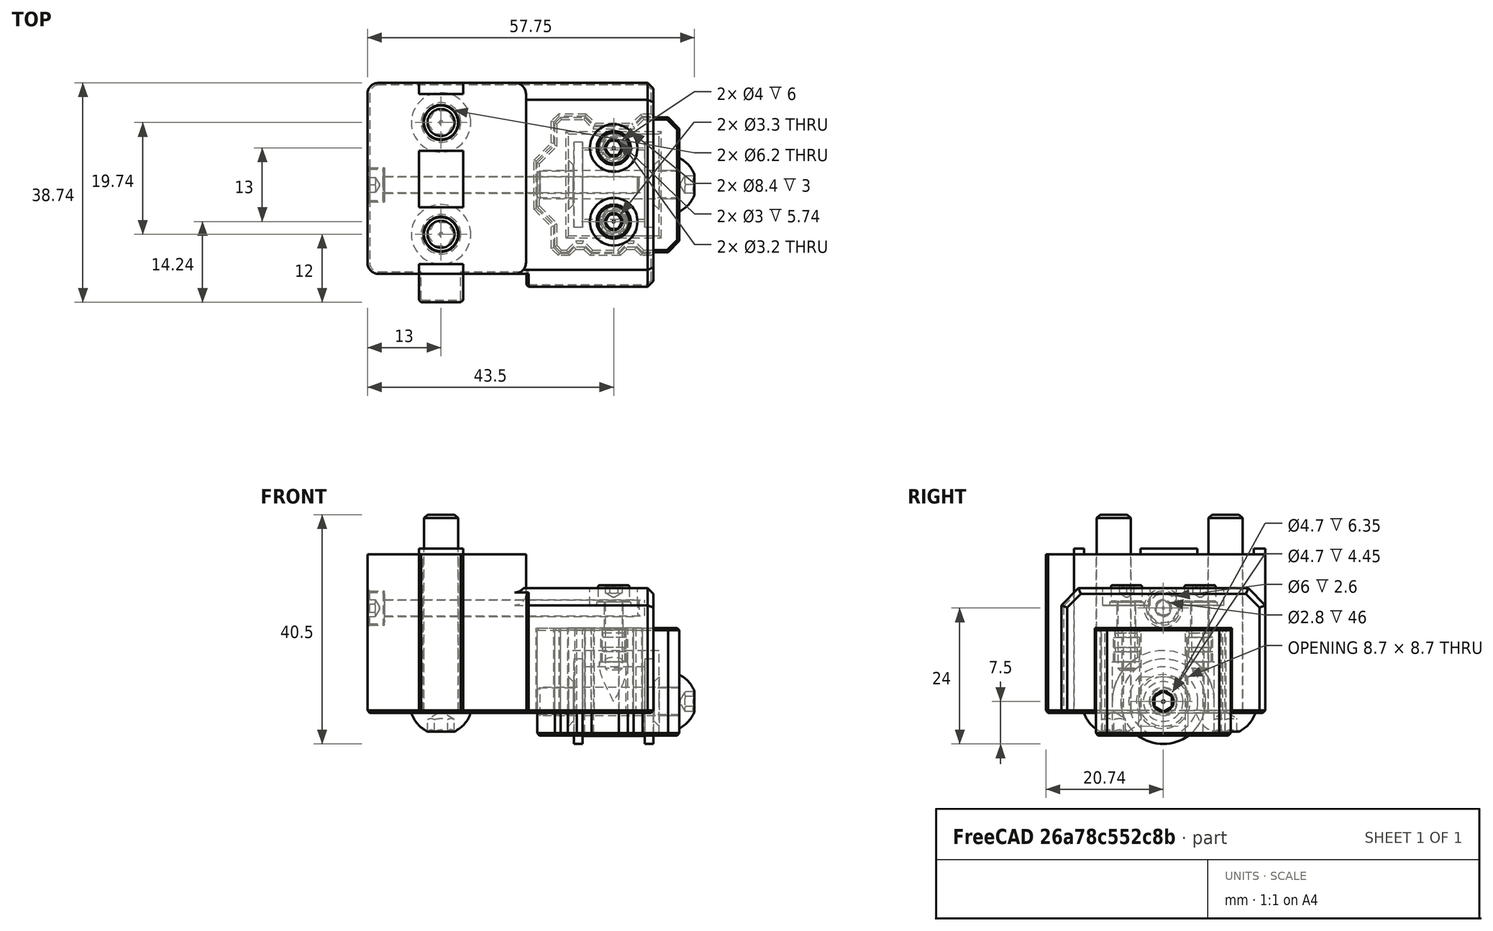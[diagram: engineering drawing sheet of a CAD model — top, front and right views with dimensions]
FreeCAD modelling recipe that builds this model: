
FCSTD DOCUMENT  (FreeCAD 0.19R24291 (Git))
Label: z-idler-left-assembly
License: Other
LicenseURL: GPL3
objects: Part::FeaturePython×10, Part::Feature×3, PartDesign::CoordinateSystem×1, App::Part×1
note: 14 computed .brp shape members not serialized (recipe doc carries the construction recipe); baked Part::Feature solids carry a one-line shape summary decoded from their .brp

FEATURE [Part::Feature] Fusion013005011003002  label="20t-9mm-idker"
  Placement = pos=(0,0,-1) rot=(0,0,1;0rad)
  shape: bbox 14 x 15 x 15 mm, 7 faces (baked)
FEATURE [Part::FeaturePython] Screw  label="M3x45-Screw"  # Fasteners workbench fastener (typed FeaturePython)
  Placement = pos=(-25,0,18.5) rot=(0,-1,0;1.5708rad)
  diameter = 4
  invert = true
  length = 10
  lengthCustom = 45
  matchOuter = true
  offset = 0
  thread = false
  type = 33
FEATURE [Part::FeaturePython] Screw001  label="M6x35-Screw"  # Fasteners workbench fastener (typed FeaturePython)
  Placement = pos=(-15,11,0) rot=(1,0,0;3.14159rad)
  diameter = 4
  invert = true
  length = 13
  lengthCustom = 35
  matchOuter = true
  offset = 0
  thread = false
  type = 39
FEATURE [Part::FeaturePython] Screw002  label="M6x35-Screw001"  # Fasteners workbench fastener (typed FeaturePython)
  Placement = pos=(-15,-8.74,0) rot=(1,0,0;3.14159rad)
  diameter = 4
  invert = true
  length = 13
  lengthCustom = 35
  matchOuter = true
  offset = 0
  thread = false
  type = 39
FEATURE [Part::FeaturePython] Washer001  label="M3-Washer006"  # Fasteners workbench fastener (typed FeaturePython)
  Placement = pos=(15.5,-6.5,19) rot=(0,0,1;0rad)
  diameter = 4
  invert = false
  matchOuter = true
  offset = 0
  type = 5
FEATURE [Part::FeaturePython] Washer  label="M3-Washer"  # Fasteners workbench fastener (typed FeaturePython)
  Placement = pos=(15.5,6.5,19) rot=(0,0,1;0rad)
  diameter = 4
  invert = false
  matchOuter = true
  offset = 0
  type = 5
FEATURE [Part::FeaturePython] Screw003  label="M3x12-Screw004"  # Fasteners workbench fastener (typed FeaturePython)
  Placement = pos=(15.5,6.5,19.55) rot=(0,0,1;0rad)
  baseObject = -> Washer [Edge1]
  diameter = 4
  invert = false
  length = 10
  lengthCustom = 12
  matchOuter = true
  offset = 0
  thread = false
  type = 33
FEATURE [Part::FeaturePython] Screw004  label="M3x12-Screw005"  # Fasteners workbench fastener (typed FeaturePython)
  Placement = pos=(15.5,-6.5,19.55) rot=(0,0,1;0rad)
  baseObject = -> Washer001 [Edge1]
  diameter = 4
  invert = false
  length = 10
  lengthCustom = 12
  matchOuter = true
  offset = 0
  thread = false
  type = 33
FEATURE [Part::FeaturePython] Screw011  label="M5x25-Screw"  # Fasteners workbench fastener (typed FeaturePython)
  Placement = pos=(27,0,2) rot=(0,1,0;1.5708rad)
  diameter = 3
  invert = true
  length = 6
  lengthCustom = 25
  matchOuter = true
  offset = 0
  thread = false
  type = 39
FEATURE [Part::Feature] Chamfer003068012003  label="z-idler-housing-left"
  Placement = pos=(0,0,-4) rot=(0,0,1;0rad)
  shape: bbox 25.1 x 23.8 x 19 mm, 95 faces (baked)
FEATURE [Part::FeaturePython] HeatSet  label="M3x4-HeatSet"  # WARN: FeaturePython — macro-defined, semantics opaque (R4)
  Placement = pos=(15.5,-6.5,9) rot=(1,0,0;3.14159rad)
  baseObject = -> Chamfer003068012003 [Edge76]
  diameter = 2
  invert = true
  offset = 6
FEATURE [Part::FeaturePython] HeatSet001  label="M3x4-HeatSet001"  # WARN: FeaturePython — macro-defined, semantics opaque (R4)
  Placement = pos=(15.5,6.5,9) rot=(1,0,0;3.14159rad)
  baseObject = -> Chamfer003068012003 [Edge77]
  diameter = 2
  invert = true
  offset = 6
FEATURE [PartDesign::CoordinateSystem] LCS_Z_idler_left  label="LCS_Z-idler-left"
  AttacherType = Attacher::AttachEngine3D
FEATURE [Part::Feature] Cut001001036010002002002001001  label="z-idler-mounter-left"
  shape: bbox 50.5 x 38.74 x 29 mm, 120 faces (baked)
FEATURE [App::Part] Part  label="Z-idler-left"
  Group = -> [Fusion013005011003002,Washer001,Screw001,Screw002,Screw003,Washer,Screw004,Screw,Screw011,Chamfer003068012003,HeatSet,HeatSet001,LCS_Z_idler_left,Cut001001036010002002002001001]
  Origin = -> Origin
